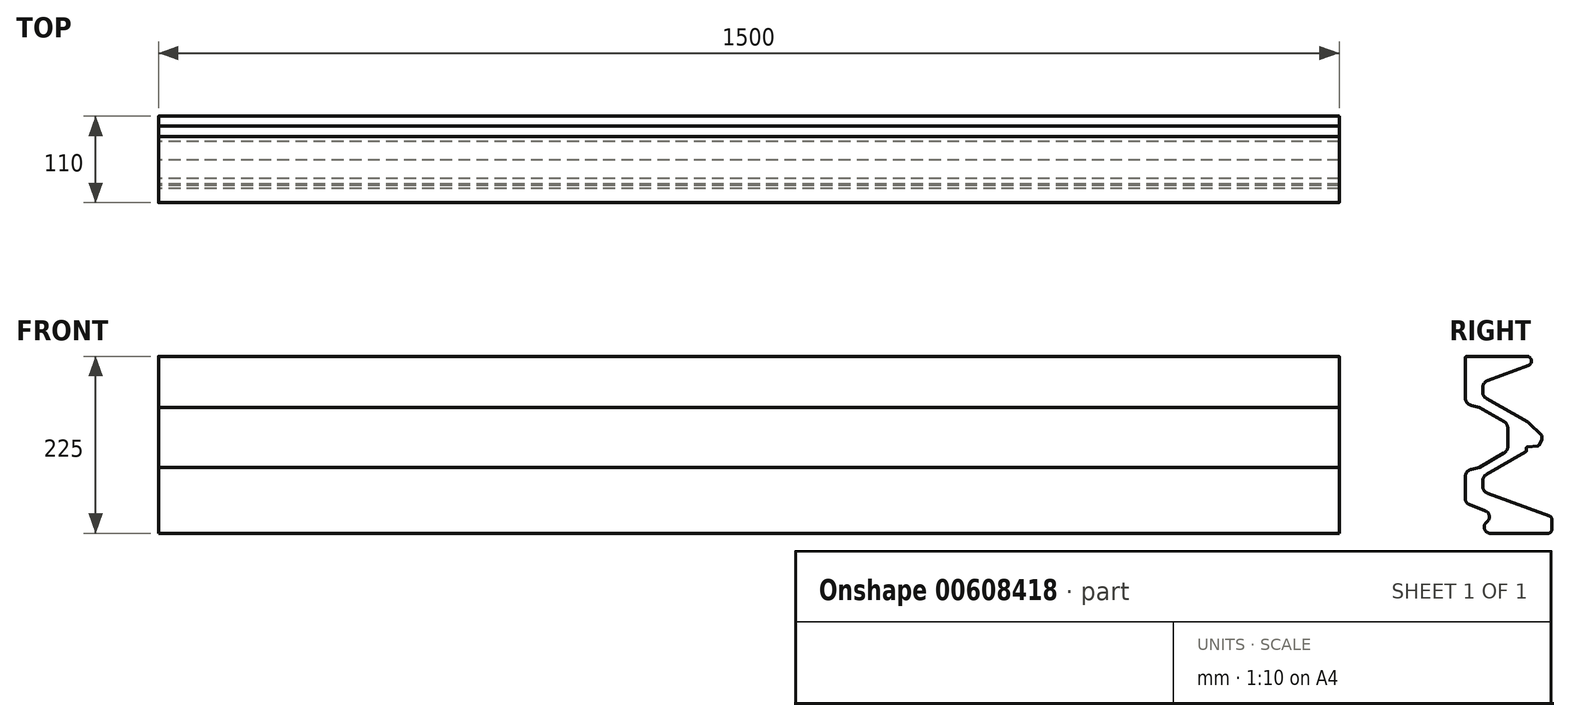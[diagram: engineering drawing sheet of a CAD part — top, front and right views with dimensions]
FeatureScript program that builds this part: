
annotation { "Feature Type Name" : "Feature", "Feature Type Description" : "" }
export const myFeature = defineFeature(function(context is Context, id is Id, definition is map)
    precondition{}
    {
        {
            var Q0;
            Q0=qCreatedBy(makeId("Right.planeOp"),FACE);
            var sketch = newSketch(context, id + "F0", { "sketchPlane" : qUnion([Q0])});
            skLineSegment(sketch, "E0", {"start": v(0, 0) * mm, "end": v(136.24, 0) * mm, "construction": true});
            skLineSegment(sketch, "E1", {"start": v(105, -122) * mm, "end": v(32, -122) * mm});
            skLineSegment(sketch, "E2", {"start": v(25.61, -93.56) * mm, "end": v(5.06, -85.44) * mm});
            skLineSegment(sketch, "E3", {"start": v(0, -78) * mm, "end": v(0, -50.3) * mm});
            skLineSegment(sketch, "E4", {"start": v(7.57, -40.6) * mm, "end": v(18, -38) * mm});
            skLineSegment(sketch, "E5", {"start": v(18, -38) * mm, "end": v(49, -20.1) * mm});
            skLineSegment(sketch, "E6", {"start": v(54, -11.44) * mm, "end": v(54, 11.44) * mm});
            skLineSegment(sketch, "E7", {"start": v(49, 20.1) * mm, "end": v(18, 38) * mm});
            skLineSegment(sketch, "E8", {"start": v(18, 38) * mm, "end": v(7.57, 40.6) * mm});
            skLineSegment(sketch, "E9", {"start": v(0, 50.3) * mm, "end": v(0, 101) * mm});
            skLineSegment(sketch, "E10", {"start": v(2, 103) * mm, "end": v(77.86, 103) * mm});
            skLineSegment(sketch, "E11", {"start": v(84, 103) * mm, "end": v(84, 92.57) * mm, "construction": true});
            skLineSegment(sketch, "E12", {"start": v(79.96, 91.1) * mm, "end": v(28.58, 72.4) * mm});
            skLineSegment(sketch, "E13", {"start": v(22, 63) * mm, "end": v(22, 57.74) * mm});
            skLineSegment(sketch, "E14", {"start": v(27, 49.2) * mm, "end": v(79.52, 19.77) * mm});
            skLineSegment(sketch, "E15", {"start": v(91.83, -11.08) * mm, "end": v(79.34, -12.06) * mm});
            skLineSegment(sketch, "E16", {"start": v(77.5, -14.05) * mm, "end": v(77.5, -16.84) * mm});
            skLineSegment(sketch, "E17", {"start": v(76.5, -18.58) * mm, "end": v(27, -47.11) * mm});
            skLineSegment(sketch, "E18", {"start": v(22, -55.78) * mm, "end": v(22, -62) * mm});
            skLineSegment(sketch, "E19", {"start": v(28.58, -71.4) * mm, "end": v(106.71, -99.83) * mm});
            skLineSegment(sketch, "E20", {"start": v(110, -104.53) * mm, "end": v(110, -117) * mm});
            skPoint(sketch, "E21.visualSharp", {"position": v(-4.27, -122) * mm});
            skArc(sketch, "E21.filletArc", {"start": v(27.34, -107.5) * mm, "mid": v(24.38, -116.45) * mm, "end": v(32, -122) * mm});
            skPoint(sketch, "E22.visualSharp", {"position": v(110, -122) * mm});
            skArc(sketch, "E22.filletArc", {"start": v(105, -122) * mm, "mid": v(108.54, -120.54) * mm, "end": v(110, -117) * mm});
            skPoint(sketch, "E23.visualSharp", {"position": v(110, -101.03) * mm});
            skArc(sketch, "E23.filletArc", {"start": v(110, -104.53) * mm, "mid": v(109.1, -101.66) * mm, "end": v(106.71, -99.83) * mm});
            skArc(sketch, "E24", {"start": v(27.34, -107.5) * mm, "mid": v(30.61, -100.02) * mm, "end": v(25.61, -93.56) * mm});
            skPoint(sketch, "E25.visualSharp", {"position": v(0, -83.44) * mm});
            skArc(sketch, "E25.filletArc", {"start": v(0, -78) * mm, "mid": v(1.39, -82.5) * mm, "end": v(5.06, -85.44) * mm});
            skLineSegment(sketch, "E26", {"start": v(80.4, 19.1) * mm, "end": v(96.91, 2.59) * mm});
            skLineSegment(sketch, "E27", {"start": v(97.5, 1.17) * mm, "end": v(97.5, -2.46) * mm});
            skLineSegment(sketch, "E28", {"start": v(97.23, -3.46) * mm, "end": v(93.4, -10.09) * mm});
            skPoint(sketch, "E29.visualSharp", {"position": v(0, -42.5) * mm});
            skArc(sketch, "E29.filletArc", {"start": v(7.57, -40.6) * mm, "mid": v(2.12, -44.15) * mm, "end": v(0, -50.3) * mm});
            skPoint(sketch, "E30.visualSharp", {"position": v(0, 42.5) * mm});
            skArc(sketch, "E30.filletArc", {"start": v(0, 50.3) * mm, "mid": v(2.12, 44.15) * mm, "end": v(7.57, 40.6) * mm});
            skPoint(sketch, "E31.visualSharp", {"position": v(54, 17.22) * mm});
            skArc(sketch, "E31.filletArc", {"start": v(54, 11.44) * mm, "mid": v(52.66, 16.44) * mm, "end": v(49, 20.1) * mm});
            skPoint(sketch, "E32.visualSharp", {"position": v(54, -17.22) * mm});
            skArc(sketch, "E32.filletArc", {"start": v(49, -20.1) * mm, "mid": v(52.66, -16.44) * mm, "end": v(54, -11.44) * mm});
            skPoint(sketch, "E33.visualSharp", {"position": v(22, 70) * mm});
            skArc(sketch, "E33.filletArc", {"start": v(28.58, 72.4) * mm, "mid": v(23.8, 68.73) * mm, "end": v(22, 63) * mm});
            skPoint(sketch, "E34.visualSharp", {"position": v(22, 52) * mm});
            skArc(sketch, "E34.filletArc", {"start": v(22, 57.74) * mm, "mid": v(23.34, 52.79) * mm, "end": v(27, 49.2) * mm});
            skPoint(sketch, "E35.visualSharp", {"position": v(22, -50) * mm});
            skArc(sketch, "E35.filletArc", {"start": v(27, -47.11) * mm, "mid": v(23.34, -50.77) * mm, "end": v(22, -55.78) * mm});
            skPoint(sketch, "E36.visualSharp", {"position": v(22, -69) * mm});
            skArc(sketch, "E36.filletArc", {"start": v(22, -62) * mm, "mid": v(23.8, -67.73) * mm, "end": v(28.58, -71.4) * mm});
            skPoint(sketch, "E37.visualSharp", {"position": v(80, 19.5) * mm});
            skArc(sketch, "E37.filletArc", {"start": v(80.4, 19.1) * mm, "mid": v(79.98, 19.47) * mm, "end": v(79.52, 19.77) * mm});
            skPoint(sketch, "E38.visualSharp", {"position": v(97.5, 2) * mm});
            skArc(sketch, "E38.filletArc", {"start": v(97.5, 1.17) * mm, "mid": v(97.35, 1.94) * mm, "end": v(96.91, 2.59) * mm});
            skPoint(sketch, "E39.visualSharp", {"position": v(97.5, -3) * mm});
            skArc(sketch, "E39.filletArc", {"start": v(97.23, -3.46) * mm, "mid": v(97.43, -2.98) * mm, "end": v(97.5, -2.46) * mm});
            skPoint(sketch, "E40.visualSharp", {"position": v(92.88, -11) * mm});
            skArc(sketch, "E40.filletArc", {"start": v(91.83, -11.08) * mm, "mid": v(92.74, -10.78) * mm, "end": v(93.4, -10.09) * mm});
            skPoint(sketch, "E41.visualSharp", {"position": v(77.5, -12.2) * mm});
            skArc(sketch, "E41.filletArc", {"start": v(79.34, -12.06) * mm, "mid": v(78.03, -12.7) * mm, "end": v(77.5, -14.05) * mm});
            skPoint(sketch, "E42.visualSharp", {"position": v(77.5, -18) * mm});
            skArc(sketch, "E42.filletArc", {"start": v(76.5, -18.58) * mm, "mid": v(77.23, -17.85) * mm, "end": v(77.5, -16.84) * mm});
            skPoint(sketch, "E43.visualSharp", {"position": v(0, 103) * mm});
            skArc(sketch, "E43.filletArc", {"start": v(2, 103) * mm, "mid": v(0.59, 102.41) * mm, "end": v(0, 101) * mm});
            skArc(sketch, "E44", {"start": v(79.96, 91.1) * mm, "mid": v(83.9, 97.93) * mm, "end": v(77.86, 103) * mm});
            skSolve(sketch);
        }
        {
            var Q0;
            Q0=makeQuery(id+"F0.imprint","IMPRINT",FACE,{"disambiguationData":[TD([[makeQuery(id+"F0.imprint","IMPRINT",EDGE,{"derivedFrom":sQuery(id+"F0.wireOp",EDGE,"E1")}),-1.0]])]});
            extrude(context, id + "F1", {"entities" : qUnion([Q0]), "depth" : 1500 * mm, "offsetDistance" : 25 * mm, "symmetric" : true});
        }
    });
